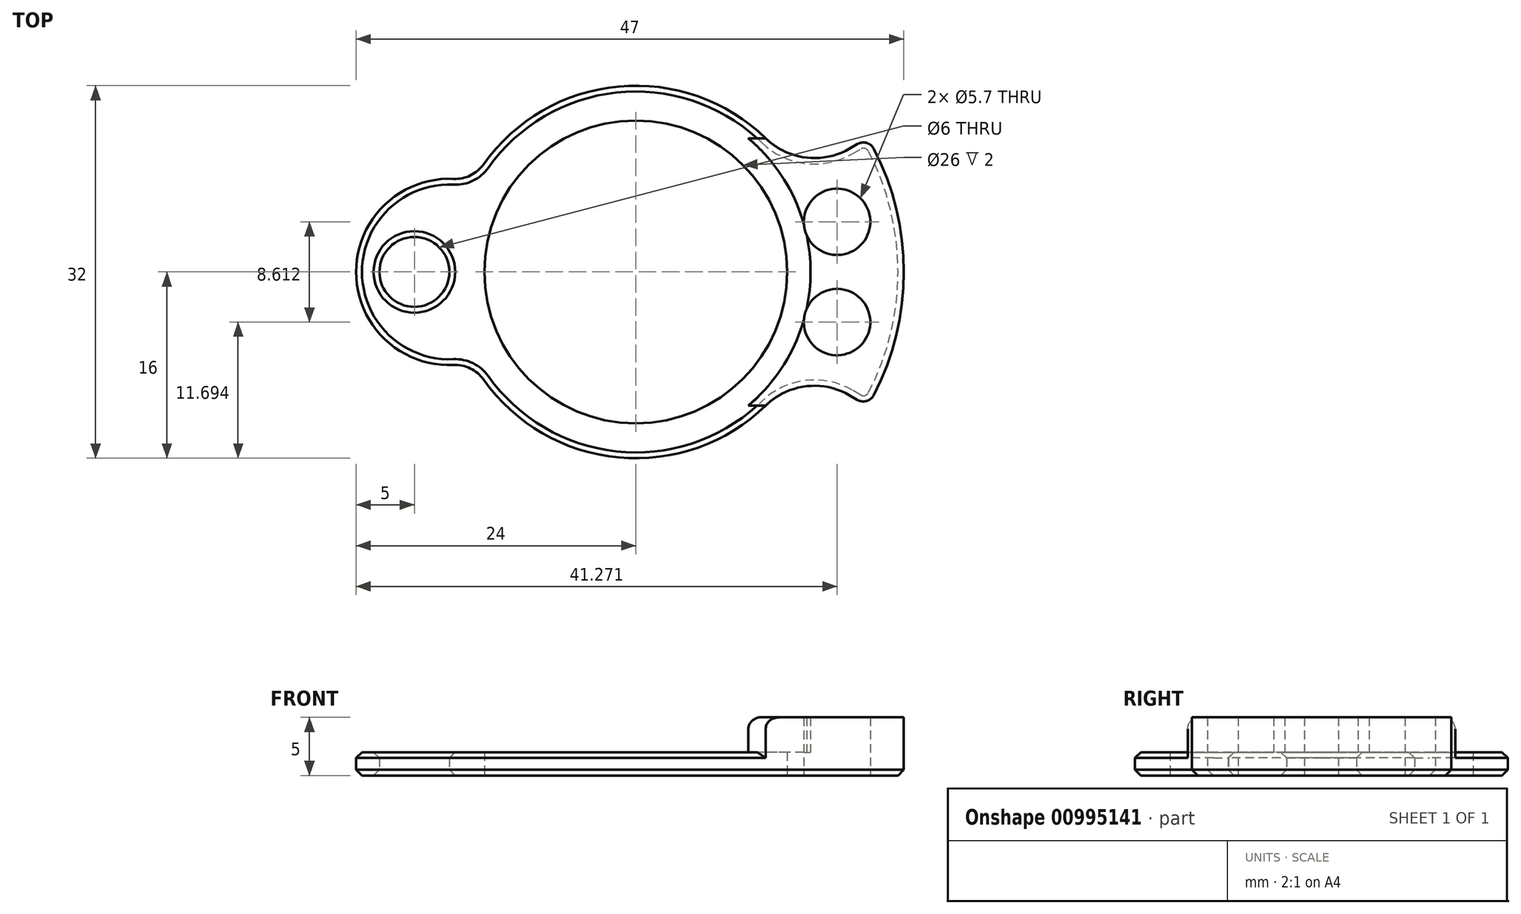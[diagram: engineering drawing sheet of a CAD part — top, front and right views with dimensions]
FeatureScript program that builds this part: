
annotation { "Feature Type Name" : "Feature", "Feature Type Description" : "" }
export const myFeature = defineFeature(function(context is Context, id is Id, definition is map)
    precondition{}
    {
        {
            var Q0;
            Q0=qCreatedBy(makeId("Top.planeOp"),FACE);
            var sketch = newSketch(context, id + "F0", { "sketchPlane" : qUnion([Q0])});
            skCircle(sketch, "E0", {"center": v(0, 0) * mm, "radius": 13 * mm});
            skArc(sketch, "E1", {"start": v(20.42, -10.58) * mm, "mid": v(23, 0) * mm, "end": v(20.42, 10.58) * mm});
            skCircle(sketch, "E2", {"center": v(17.27, 4.3) * mm, "radius": 2.85 * mm});
            skCircle(sketch, "E3", {"center": v(17.27, -4.3) * mm, "radius": 2.85 * mm});
            skLineSegment(sketch, "E4", {"start": v(-30.9, 0) * mm, "end": v(29.78, 0) * mm, "construction": true});
            skLineSegment(sketch, "E5", {"start": v(0, 0) * mm, "end": v(19.92, 11.5) * mm, "construction": true});
            skLineSegment(sketch, "E6", {"start": v(18.33, 10.58) * mm, "end": v(19.03, 10.99) * mm});
            skLineSegment(sketch, "E7", {"start": v(18.33, -10.58) * mm, "end": v(19.03, -10.99) * mm});
            skCircle(sketch, "E8", {"center": v(17.27, 4.3) * mm, "radius": 3.8 * mm, "construction": true});
            skLineSegment(sketch, "E9", {"start": v(0, 0) * mm, "end": v(33.34, 8.31) * mm, "construction": true});
            skArc(sketch, "E10", {"start": v(11.15, 11.48) * mm, "mid": v(-1.46, 15.93) * mm, "end": v(-13.05, 9.25) * mm});
            skLineSegment(sketch, "E11", {"start": v(19.92, 11.5) * mm, "end": v(26.2, 15.12) * mm, "construction": true});
            skPoint(sketch, "E12", {"position": v(0, 16) * mm});
            skPoint(sketch, "E13", {"position": v(0, -16) * mm});
            skPoint(sketch, "E14", {"position": v(20.96, 5.23) * mm});
            skPoint(sketch, "E15.visualSharp", {"position": v(19.92, 11.5) * mm});
            skArc(sketch, "E15.filletArc", {"start": v(20.42, 10.58) * mm, "mid": v(19.81, 11.08) * mm, "end": v(19.03, 10.99) * mm});
            skPoint(sketch, "E16.visualSharp", {"position": v(19.92, -11.5) * mm});
            skArc(sketch, "E16.filletArc", {"start": v(19.03, -10.99) * mm, "mid": v(19.81, -11.08) * mm, "end": v(20.42, -10.58) * mm});
            skPoint(sketch, "E17.visualSharp", {"position": v(13.86, 8) * mm});
            skArc(sketch, "E17.filletArc", {"start": v(11.15, 11.48) * mm, "mid": v(14.6, 9.82) * mm, "end": v(18.33, 10.58) * mm});
            skPoint(sketch, "E18.visualSharp", {"position": v(13.86, -8) * mm});
            skArc(sketch, "E18.filletArc", {"start": v(18.33, -10.58) * mm, "mid": v(14.6, -9.82) * mm, "end": v(11.15, -11.48) * mm});
            skArc(sketch, "E19", {"start": v(-15.64, 8) * mm, "mid": v(-24, 0) * mm, "end": v(-15.64, -8) * mm});
            skCircle(sketch, "E20", {"center": v(-19, 0) * mm, "radius": 3 * mm});
            skArc(sketch, "E21.trimOffspring", {"start": v(-13.05, -9.25) * mm, "mid": v(-1.46, -15.93) * mm, "end": v(11.15, -11.48) * mm});
            skPoint(sketch, "E22.visualSharp", {"position": v(-14, 7.75) * mm});
            skArc(sketch, "E22.filletArc", {"start": v(-15.64, 8) * mm, "mid": v(-14.18, 8.3) * mm, "end": v(-13.05, 9.25) * mm});
            skPoint(sketch, "E23.visualSharp", {"position": v(-14, -7.75) * mm});
            skArc(sketch, "E23.filletArc", {"start": v(-13.05, -9.25) * mm, "mid": v(-14.18, -8.3) * mm, "end": v(-15.64, -8) * mm});
            skCircle(sketch, "E24", {"center": v(0, 0) * mm, "radius": 15 * mm});
            skLineSegment(sketch, "E25", {"start": v(11.15, 11.48) * mm, "end": v(9.66, 11.48) * mm});
            skLineSegment(sketch, "E26", {"start": v(11.15, -11.48) * mm, "end": v(9.66, -11.48) * mm});
            skSolve(sketch);
        }
        {
            var Q0;
            Q0=makeQuery(id+"F0.imprint","IMPRINT",FACE,{"disambiguationData":[TD([[makeQuery(id+"F0.imprint","IMPRINT",EDGE,{"derivedFrom":sQuery(id+"F0.wireOp",EDGE,"E1")}),1.0]])]});
            extrude(context, id + "F1", {"entities" : qUnion([Q0]), "depth" : 5 * mm, "offsetDistance" : 25 * mm});
        }
        {
            var Q0;
            Q0=makeQuery(id+"F0.imprint","IMPRINT",FACE,{"disambiguationData":[TD([[makeQuery(id+"F0.imprint","IMPRINT",EDGE,{"derivedFrom":sQuery(id+"F0.wireOp",EDGE,"E10")}),1.0]])]});
            var Q1;
            Q1=makeQuery(id+"F0.imprint","IMPRINT",FACE,{"disambiguationData":[TD([[makeQuery(id+"F0.imprint","IMPRINT",EDGE,{"derivedFrom":sQuery(id+"F0.wireOp",EDGE,"E0")}),-1.0]])]});
            extrude(context, id + "F2", {"entities" : qUnion([Q0, Q1]), "operationType" : NewBodyOperationType.ADD, "depth" : 2 * mm, "offsetDistance" : 25 * mm});
        }
        {
            var Q0;
            Q0=makeQuery(id+"F1.opExtrude","CAP_EDGE",EDGE,{"disambiguationData":[OSD([sQuery(id+"F0.wireOp",EDGE,"E26")])],"isStart":false});
            var Q1;
            Q1=makeQuery(id+"F1.opExtrude","CAP_EDGE",EDGE,{"disambiguationData":[OSD([sQuery(id+"F0.wireOp",EDGE,"E25")])],"isStart":false});
            var Q2;
            Q2=makeQuery(id+"F2.opExtrude","CAP_EDGE",EDGE,{"disambiguationData":[OSD([sQuery(id+"F0.wireOp",EDGE,"E25")])],"isStart":false});
            var Q3;
            Q3=makeQuery(id+"F2.opExtrude","CAP_EDGE",EDGE,{"disambiguationData":[OSD([sQuery(id+"F0.wireOp",EDGE,"E26")])],"isStart":false});
            fillet(context, id + "F3", {"entities" : qUnion([Q0, Q1, Q2, Q3]), "radius" : 1 * mm, "tangentPropagation" : true, "allowEdgeOverflow" : false});
        }
        {
            var Q0;
            Q0=makeQuery(id+"F2.opExtrude","CAP_EDGE",EDGE,{"disambiguationData":[OSD([sQuery(id+"F0.wireOp",EDGE,"E10")])],"isStart":true});
            var Q1;
            Q1=makeQuery(id+"F2.opExtrude","CAP_EDGE",EDGE,{"disambiguationData":[OSD([sQuery(id+"F0.wireOp",EDGE,"E19")])],"isStart":false});
            var Q2;
            Q2=makeQuery(id+"F2.opExtrude","CAP_EDGE",EDGE,{"disambiguationData":[OSD([sQuery(id+"F0.wireOp",EDGE,"E20")])],"isStart":false});
            var Q3;
            Q3=makeQuery(id+"F2.opExtrude","CAP_EDGE",EDGE,{"disambiguationData":[OSD([sQuery(id+"F0.wireOp",EDGE,"E20")])],"isStart":true});
            chamfer(context, id + "F4", {"entities" : qUnion([Q0, Q1, Q2, Q3]), "width" : 0.5 * mm, "tangentPropagation" : true});
        }
    });
